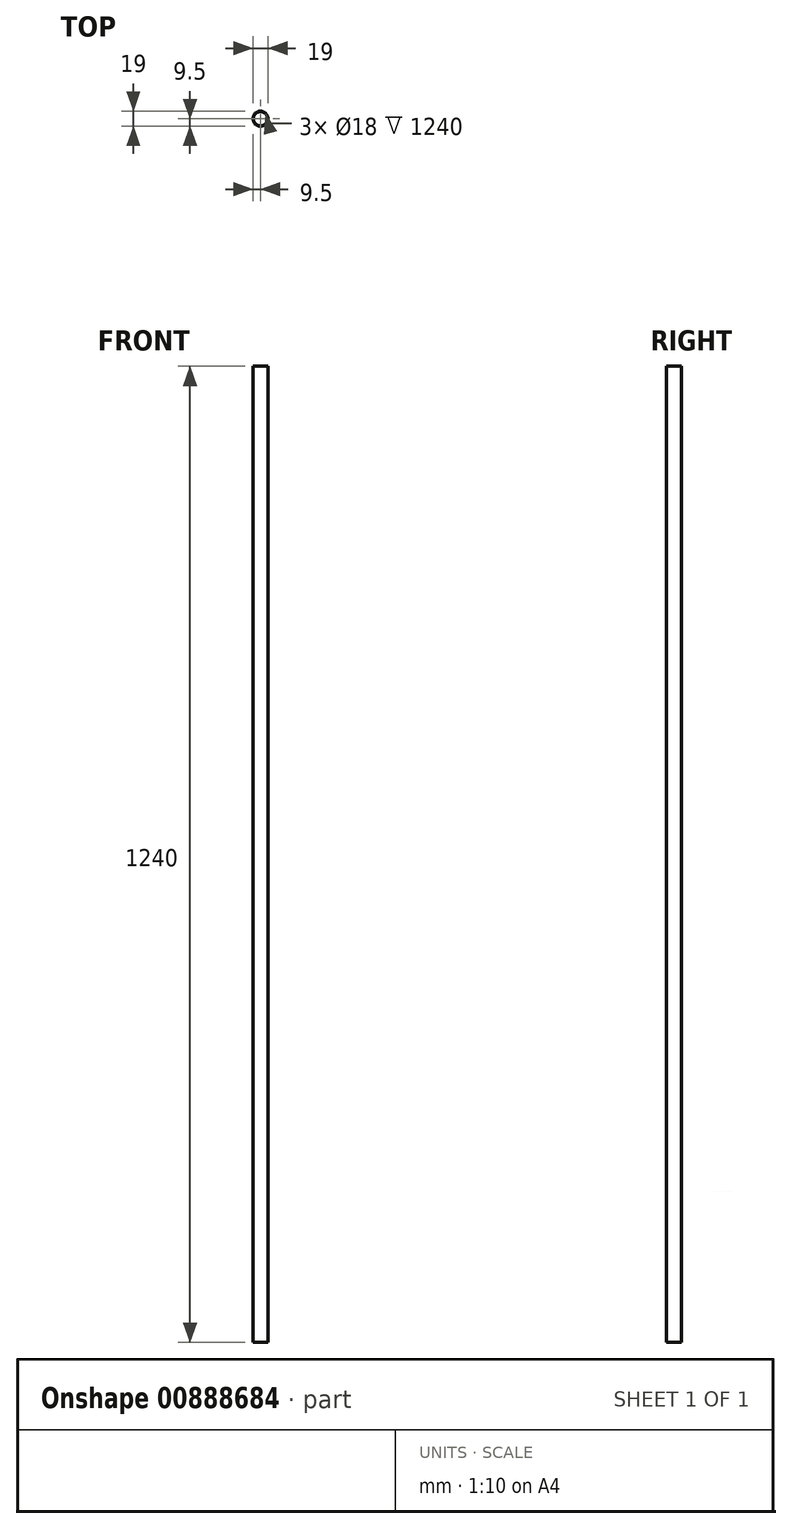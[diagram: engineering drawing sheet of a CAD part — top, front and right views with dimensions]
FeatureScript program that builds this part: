
annotation { "Feature Type Name" : "Feature", "Feature Type Description" : "" }
export const myFeature = defineFeature(function(context is Context, id is Id, definition is map)
    precondition{}
    {
        {
            var Q0;
            Q0=qCreatedBy(makeId("Top.planeOp"),FACE);
            var sketch = newSketch(context, id + "F0", { "sketchPlane" : qUnion([Q0])});
            skCircle(sketch, "E0", {"center": v(0, 0) * mm, "radius": 9.5 * mm});
            skCircle(sketch, "E1", {"center": v(0, 0) * mm, "radius": 9 * mm});
            skSolve(sketch);
        }
        {
            var Q0;
            Q0=makeQuery(id+"F0.imprint","IMPRINT",FACE,{"disambiguationData":[TD([[makeQuery(id+"F0.imprint","IMPRINT",EDGE,{"derivedFrom":sQuery(id+"F0.wireOp",EDGE,"E0")}),1.0]])]});
            extrude(context, id + "F1", {"entities" : qUnion([Q0]), "oppositeDirection" : true, "depth" : 1240 * mm, "offsetDistance" : 25 * mm});
        }
    });
